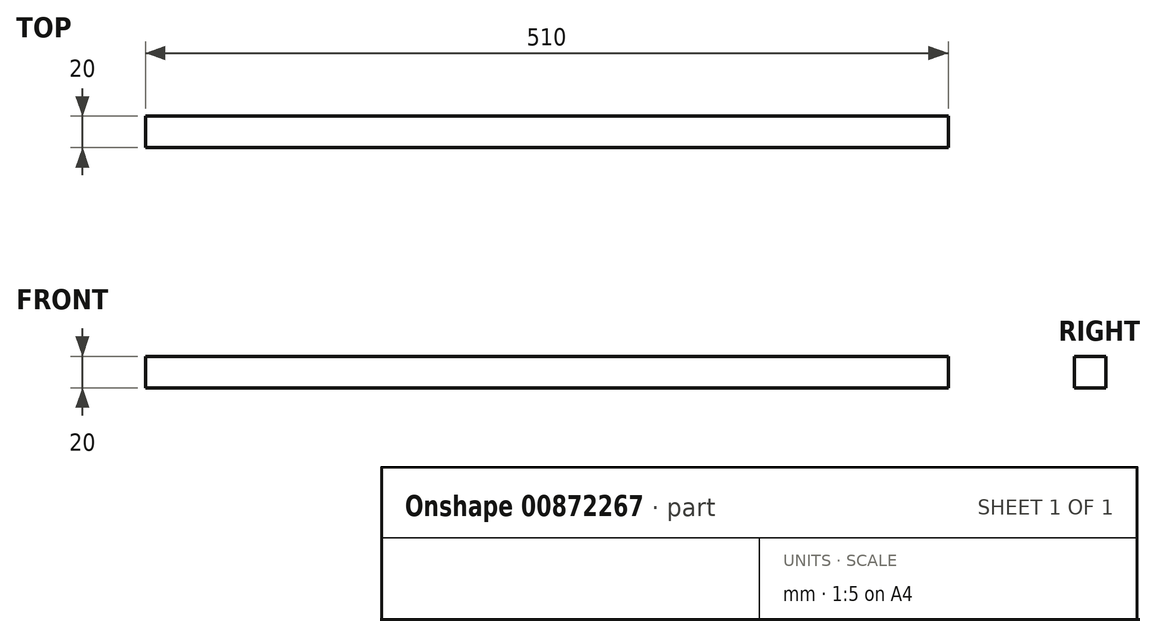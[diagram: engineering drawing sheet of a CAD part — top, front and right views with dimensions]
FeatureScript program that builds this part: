
annotation { "Feature Type Name" : "Feature", "Feature Type Description" : "" }
export const myFeature = defineFeature(function(context is Context, id is Id, definition is map)
    precondition{}
    {
        {
            var Q0;
            Q0=qCreatedBy(makeId("Front.planeOp"),FACE);
            var sketch = newSketch(context, id + "F0", { "sketchPlane" : qUnion([Q0])});
            skLineSegment(sketch, "E0.bottom", {"start": v(255, -10) * mm, "end": v(-255, -10) * mm});
            skLineSegment(sketch, "E0.top", {"start": v(255, 10) * mm, "end": v(-255, 10) * mm});
            skLineSegment(sketch, "E0.left", {"start": v(255, -10) * mm, "end": v(255, 10) * mm});
            skLineSegment(sketch, "E0.right", {"start": v(-255, -10) * mm, "end": v(-255, 10) * mm});
            skPoint(sketch, "E0.middle", {"position": v(0, 0) * mm});
            skSolve(sketch);
        }
        {
            var Q0;
            Q0=makeQuery(id+"F0.imprint","IMPRINT",FACE,{"disambiguationData":[TD([[makeQuery(id+"F0.imprint","IMPRINT",EDGE,{"derivedFrom":sQuery(id+"F0.wireOp",EDGE,"E0.bottom")}),-1.0]])]});
            extrude(context, id + "F1", {"entities" : qUnion([Q0]), "endBound" : BoundingType.SYMMETRIC, "depth" : 20 * mm, "offsetDistance" : 25 * mm});
        }
    });
